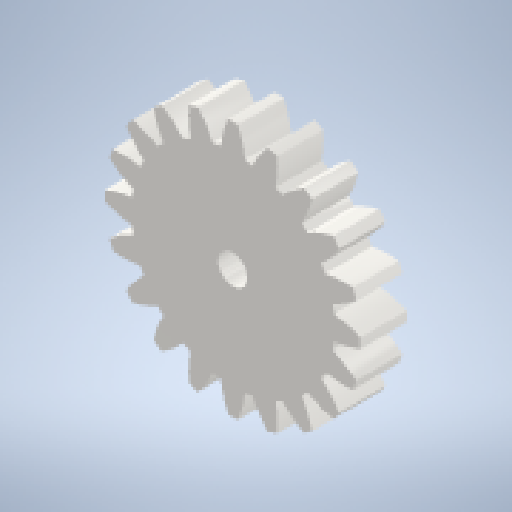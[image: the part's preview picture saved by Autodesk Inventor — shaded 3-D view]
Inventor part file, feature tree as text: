
AUTODESK INVENTOR PART (.ipt)
format: ipt  version: 2024 (Build 280153000, 153)  size: 250,368 bytes
history: native  units: mm (DEFAULTED — no unit token found)
features: plane x3, other x3, extrude x2, sketch x2
ambient origin geometry x8: Origin, YZ Plane, XZ Plane, XY Plane, X Axis, Y Axis, Z Axis, Center Point
bodies: Solid1 (feature_tree)
feature tree (10):
  extrude  "Extrusion1"  Depth=3.175mm TaperAngle=0.0deg
  plane  "Work Plane1"
  plane  "Work Plane2"
  plane  "Work Plane3"
  other  "Spur Gear"
  extrude  "Extrusion2"  Depth=76.2mm TaperAngle=0.0deg
  sketch  "Sketch1"  dims[d0=17.462215mm d1=3.175mm d2=0.0mm]
  other  "Srf1"
  sketch  "Sketch3"  dims[d3=15.875mm d4=76.2mm d5=0.0mm d6=0.0mm d7=1.570796mm d9=0.0mm d14=0.0mm d15=32.1818mm d16=0.0mm d17=0.0mm d18=0.0mm d19=32.1818mm d20=2.0mm d21=25.4mm d22=0.0mm]
  other  "Pitch Diameter"
